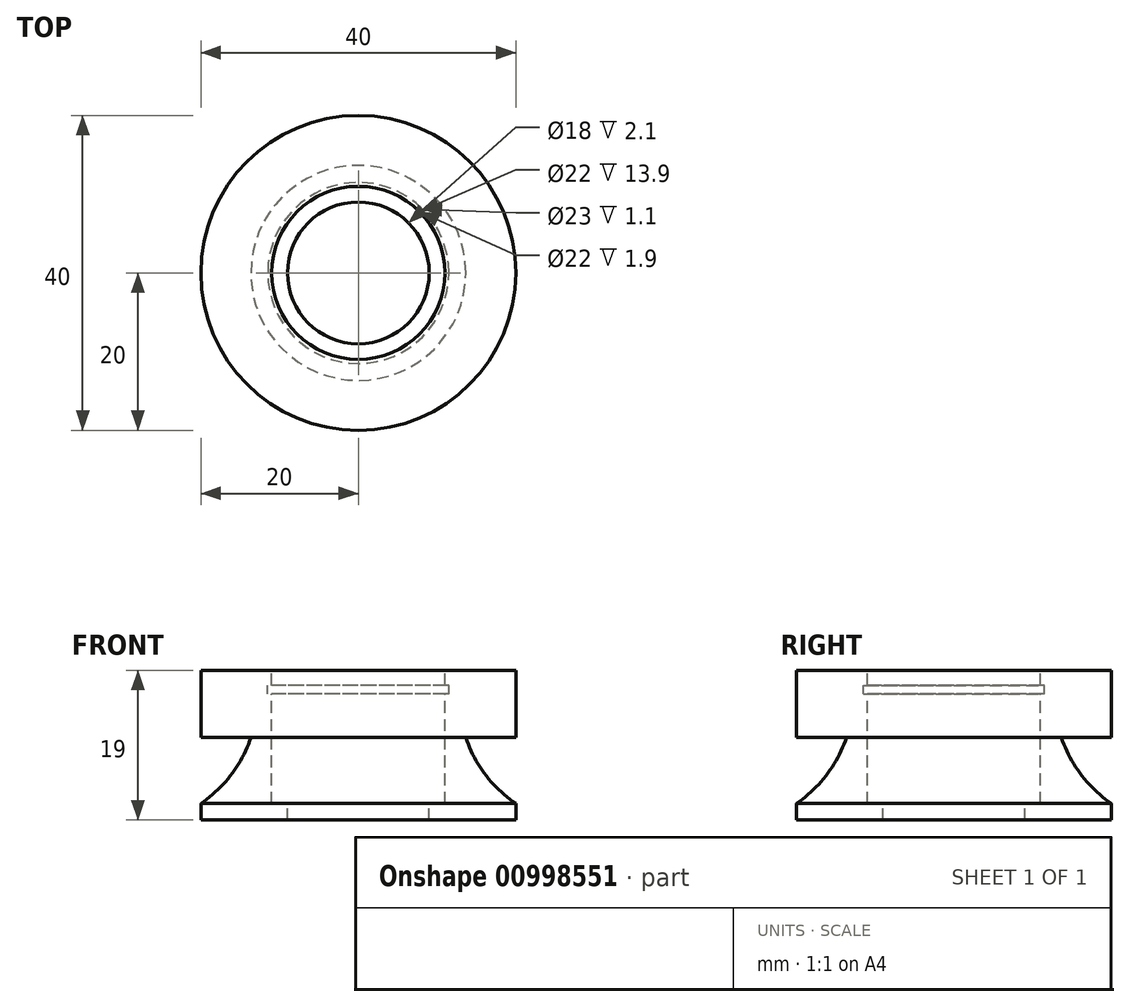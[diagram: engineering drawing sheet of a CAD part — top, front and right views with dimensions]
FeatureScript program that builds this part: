
annotation { "Feature Type Name" : "Feature", "Feature Type Description" : "" }
export const myFeature = defineFeature(function(context is Context, id is Id, definition is map)
    precondition{}
    {
        {
            var Q0;
            Q0=qCreatedBy(makeId("Front.planeOp"),FACE);
            var sketch = newSketch(context, id + "F0", { "sketchPlane" : qUnion([Q0])});
            skLineSegment(sketch, "E0.bottom", {"start": v(-40, -10.49) * mm, "end": v(-31, -10.49) * mm});
            skLineSegment(sketch, "E0.top", {"start": v(-40, -29.49) * mm, "end": v(-29, -29.49) * mm});
            skLineSegment(sketch, "E0.left", {"start": v(-40, -10.49) * mm, "end": v(-40, -18.99) * mm});
            skLineSegment(sketch, "E1", {"start": v(-40, -18.99) * mm, "end": v(-33.65, -18.99) * mm});
            skPoint(sketch, "E1.endSnap0", {"position": v(-20, -19.99) * mm});
            skLineSegment(sketch, "E2", {"start": v(-40, -29.49) * mm, "end": v(-40, -27.39) * mm});
            skPoint(sketch, "E0.right.end.orphan", {"position": v(0, -29.49) * mm});
            skPoint(sketch, "E0.right.start.orphan", {"position": v(0, -10.49) * mm});
            skArc(sketch, "E3", {"start": v(-40, -27.39) * mm, "mid": v(-36.13, -23.71) * mm, "end": v(-33.65, -18.99) * mm});
            skLineSegment(sketch, "E4.trimOffspring", {"start": v(-40, -27.39) * mm, "end": v(-40, -29.49) * mm});
            skPoint(sketch, "E5.start.orphan", {"position": v(-20, -18.99) * mm});
            skLineSegment(sketch, "E6", {"start": v(-31, -10.49) * mm, "end": v(-31, -12.39) * mm});
            skLineSegment(sketch, "E7", {"start": v(-31, -27.39) * mm, "end": v(-29, -27.39) * mm});
            skLineSegment(sketch, "E8", {"start": v(-31, -12.39) * mm, "end": v(-31.5, -12.39) * mm});
            skLineSegment(sketch, "E9", {"start": v(-31.5, -12.39) * mm, "end": v(-31.5, -13.49) * mm});
            skLineSegment(sketch, "E10", {"start": v(-31.5, -13.49) * mm, "end": v(-31, -13.49) * mm});
            skLineSegment(sketch, "E11.trimOffspring", {"start": v(-31, -13.49) * mm, "end": v(-31, -27.39) * mm});
            skPoint(sketch, "E12.start.orphan", {"position": v(-20, -10.49) * mm});
            skLineSegment(sketch, "E13", {"start": v(-29, -29.49) * mm, "end": v(-29, -27.39) * mm});
            skPoint(sketch, "E14.trimOffspring.end.orphan", {"position": v(-20, -29.49) * mm});
            skPoint(sketch, "E14.trimOffspring.start.orphan", {"position": v(-20, -27.39) * mm});
            skLineSegment(sketch, "E15", {"start": v(-20, -10.49) * mm, "end": v(-20, -29.49) * mm});
            skSolve(sketch);
        }
        {
            var Q0;
            Q0=makeQuery(id+"F0.imprint","IMPRINT",FACE,{"disambiguationData":[TD([[makeQuery(id+"F0.imprint","IMPRINT",EDGE,{"derivedFrom":sQuery(id+"F0.wireOp",EDGE,"E0.bottom")}),-1.0]])]});
            var Q1;
            Q1=sQuery(id+"F0.wireOp",EDGE,"E15");
            revolve(context, id + "F1", {"surfaceOperationType" : NewSurfaceOperationType.NEW, "entities" : qUnion([Q0]), "axis" : qUnion([Q1]), "revolveType" : RevolveType.FULL});
        }
    });
